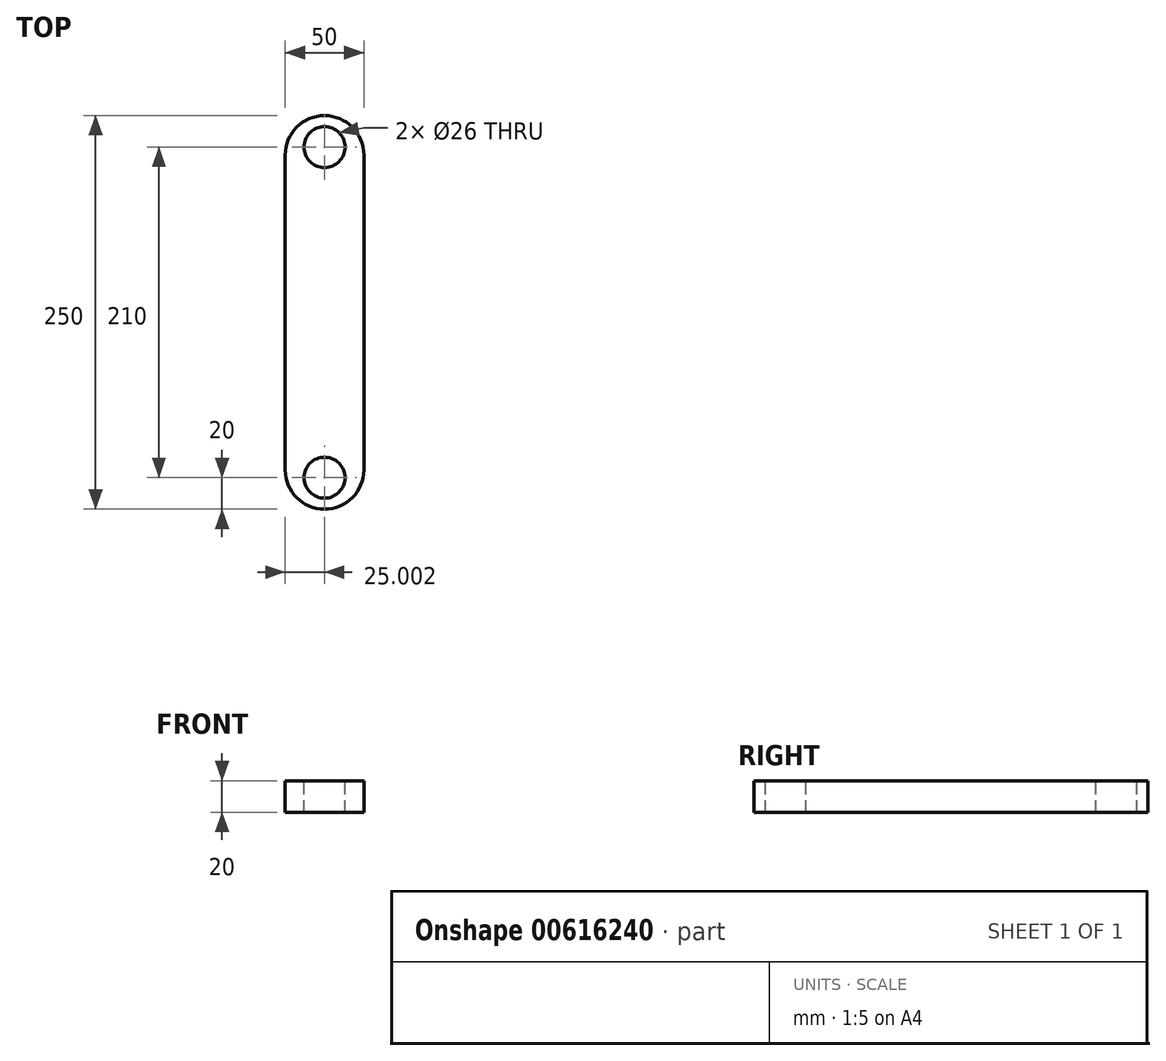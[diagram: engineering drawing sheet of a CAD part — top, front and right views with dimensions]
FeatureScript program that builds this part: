
annotation { "Feature Type Name" : "Feature", "Feature Type Description" : "" }
export const myFeature = defineFeature(function(context is Context, id is Id, definition is map)
    precondition{}
    {
        {
            var Q0;
            Q0=qCreatedBy(makeId("Front.planeOp"),FACE);
            var sketch = newSketch(context, id + "F0", { "sketchPlane" : qUnion([Q0])});
            skLineSegment(sketch, "E0", {"start": v(-28.45, 0) * mm, "end": v(-28.45, 1.13) * mm});
            skLineSegment(sketch, "E1", {"start": v(-28.45, 1.13) * mm, "end": v(21.55, 1.13) * mm});
            skLineSegment(sketch, "E2", {"start": v(21.55, 1.13) * mm, "end": v(21.55, -18.87) * mm});
            skLineSegment(sketch, "E3", {"start": v(21.55, -18.87) * mm, "end": v(-28.45, -18.87) * mm});
            skLineSegment(sketch, "E4", {"start": v(-28.45, -18.87) * mm, "end": v(-28.45, 0) * mm});
            skSolve(sketch);
        }
        {
            var Q0;
            Q0=makeQuery(id+"F0.imprint","IMPRINT",FACE,{"disambiguationData":[TD([[makeQuery(id+"F0.imprint","IMPRINT",EDGE,{"derivedFrom":sQuery(id+"F0.wireOp",EDGE,"E0")}),-1.0]])]});
            extrude(context, id + "F1", {"entities" : qUnion([Q0]), "depth" : 250 * mm, "offsetDistance" : 25 * mm});
        }
        {
            var Q0;
            Q0=makeQuery(id+"F1.opExtrude","SWEPT_FACE",FACE,{"disambiguationData":[OSD([sQuery(id+"F0.wireOp",EDGE,"E1")])]});
            var sketch = newSketch(context, id + "F2", { "sketchPlane" : qUnion([Q0])});
            skArc(sketch, "E5", {"start": v(-28.45, -225) * mm, "mid": v(-3.45, -250) * mm, "end": v(21.55, -225) * mm});
            skLineSegment(sketch, "E6", {"start": v(-28.45, -225) * mm, "end": v(-28.45, -250) * mm});
            skLineSegment(sketch, "E7", {"start": v(-28.45, -250) * mm, "end": v(21.55, -250) * mm});
            skLineSegment(sketch, "E8", {"start": v(21.55, -250) * mm, "end": v(21.55, -225) * mm});
            skArc(sketch, "E9", {"start": v(21.55, -25) * mm, "mid": v(-3.45, 0) * mm, "end": v(-28.45, -25) * mm});
            skLineSegment(sketch, "E10", {"start": v(-28.45, -25) * mm, "end": v(-28.45, 0) * mm});
            skLineSegment(sketch, "E11", {"start": v(-28.45, 0) * mm, "end": v(21.55, 0) * mm});
            skLineSegment(sketch, "E12", {"start": v(21.55, 0) * mm, "end": v(21.55, -25) * mm});
            skSolve(sketch);
        }
        {
            var Q0;
            {var subQ0=sQuery(id+"F2.wireOp",EDGE,"E12");Q0=makeQuery(id+"F2.imprint","IMPRINT",FACE,{"disambiguationData":[TD([[makeQuery(id+"F2.imprint","IMPRINT",EDGE,{"derivedFrom":subQ0}),1.0]])]});}
            var Q1;
            {var subQ0=sQuery(id+"F2.wireOp",EDGE,"E10");Q1=makeQuery(id+"F2.imprint","IMPRINT",FACE,{"disambiguationData":[TD([[makeQuery(id+"F2.imprint","IMPRINT",EDGE,{"derivedFrom":subQ0}),-1.0]])]});}
            var Q2;
            {var subQ0=sQuery(id+"F2.wireOp",EDGE,"E8");Q2=makeQuery(id+"F2.imprint","IMPRINT",FACE,{"disambiguationData":[TD([[makeQuery(id+"F2.imprint","IMPRINT",EDGE,{"derivedFrom":subQ0}),1.0]])]});}
            var Q3;
            {var subQ0=sQuery(id+"F2.wireOp",EDGE,"E6");Q3=makeQuery(id+"F2.imprint","IMPRINT",FACE,{"disambiguationData":[TD([[makeQuery(id+"F2.imprint","IMPRINT",EDGE,{"derivedFrom":subQ0}),-1.0]])]});}
            extrude(context, id + "F3", {"entities" : qUnion([Q0, Q1, Q2, Q3]), "operationType" : NewBodyOperationType.REMOVE, "oppositeDirection" : true, "depth" : 25 * mm, "offsetDistance" : 25 * mm});
        }
        {
            var Q0;
            Q0=makeQuery(id+"F1.opExtrude","SWEPT_FACE",FACE,{"disambiguationData":[OSD([sQuery(id+"F0.wireOp",EDGE,"E1")])]});
            var sketch = newSketch(context, id + "F4", { "sketchPlane" : qUnion([Q0])});
            skPoint(sketch, "E13.endSnap0", {"position": v(-3.45, 0) * mm});
            skCircle(sketch, "E14", {"center": v(-3.45, -230) * mm, "radius": 13 * mm});
            skCircle(sketch, "E15", {"center": v(-3.45, -20) * mm, "radius": 13 * mm});
            skSolve(sketch);
        }
        {
            var Q0;
            Q0=makeQuery(id+"F4.imprint","IMPRINT",FACE,{"disambiguationData":[TD([[makeQuery(id+"F4.imprint","IMPRINT",EDGE,{"derivedFrom":sQuery(id+"F4.wireOp",EDGE,"E15")}),1.0]])]});
            var Q1;
            Q1=makeQuery(id+"F4.imprint","IMPRINT",FACE,{"disambiguationData":[TD([[makeQuery(id+"F4.imprint","IMPRINT",EDGE,{"derivedFrom":sQuery(id+"F4.wireOp",EDGE,"E14")}),1.0]])]});
            extrude(context, id + "F5", {"entities" : qUnion([Q0, Q1]), "operationType" : NewBodyOperationType.REMOVE, "oppositeDirection" : true, "depth" : 25 * mm, "offsetDistance" : 25 * mm});
        }
    });
